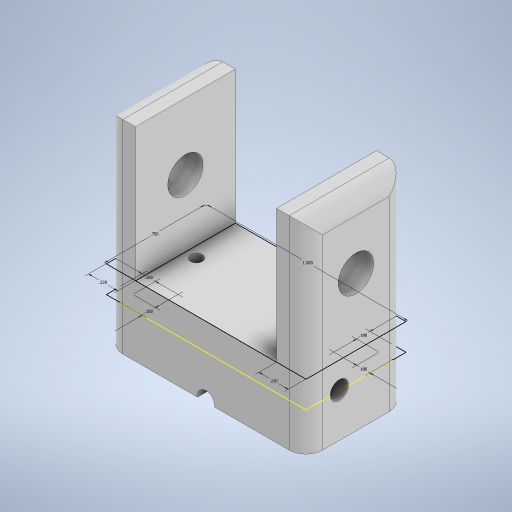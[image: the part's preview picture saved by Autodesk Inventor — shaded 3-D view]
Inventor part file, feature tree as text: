
AUTODESK INVENTOR PART (.ipt)
format: ipt  version: 2024.1 (Build 281209000, 209)  size: 327,680 bytes
history: native  units: in
note: dims shown in document units (in); Inventor stores cm internally (conversion verified against a paired STEP export)
features: extrude x4, hole x4, sketch x4, fillet x1
ambient origin geometry x8: Origin, YZ Plane, XZ Plane, XY Plane, X Axis, Y Axis, Z Axis, Center Point
bodies: Solid1 (feature_tree)
feature tree (13):
  extrude  "Extrusion1"  Depth=0.75in
  extrude  "Extrusion2"  Depth=0.22in
  hole  "Hole1"  [1 undecoded]
  sketch  "Sketch3"  dims[d0=1.5in d1=0.75in]
  extrude  "Extrusion3"  Depth=0.1in
  extrude  "Extrusion4"  Depth=0.1in
  hole  "Hole2"  [1 undecoded]
  hole  "Hole3"  [1 undecoded]
  hole  "Hole4"  [1 undecoded]
  fillet  "Fillet1"  Radius=0.325in
  sketch  "Sketch4"  dims[d2=0.22in d3=0.22in]
  sketch  "Sketch5"  dims[d4=1.0in d5=0.0in d6=0.2in d7=0.0in]
  sketch  "Sketch6"  dims[d8=0.5in d9=0.266in d10=0.75in d11=0.438in d12=0.25in d13=0.5635in d14=1.0in d15=0.8108in d16=0.1in d17=0.1in d18=0.1in d19=0.1in d20=0.1in d21=0.0in d22=0.325in d23=0.0in d24=0.5in d25=180.0deg d26=0.136in d27=0.75in d28=0.375in d29=0.25in d30=0.5635in d31=1.0in d32=0.0in d33=0.275in d34=1.165in d35=0.3in d36=0.4475in d37=0.895in d38=0.089in d39=0.75in d40=0.375in d41=0.25in d42=0.5635in d43=1.0in d44=0.0in d45=0.415in d46=0.13in d47=0.75in d48=0.375in d49=0.25in d50=0.5635in d51=1.0in d52=0.0in d53=0.125in]
note: 4 required parameter values undecoded (feature->parameter linkage not recoverable at this tier; creation-order binding heuristic only, values carry confidence <= 0.55)
